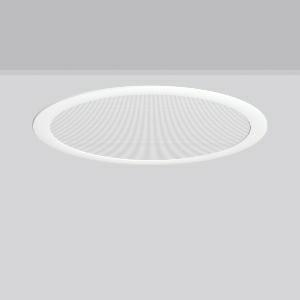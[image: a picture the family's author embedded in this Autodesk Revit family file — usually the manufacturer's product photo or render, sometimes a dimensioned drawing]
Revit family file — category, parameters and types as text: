
# Revit family: toledo_flat_round_e_901586_002_e46f
name_source: partatom
category: Lighting Fixtures
units: mm (PartAtom-declared; Revit-internal decimal feet)

## family parameters
Cut with Voids When Loaded = No
Host = Face
Light Source = No
Part Type = Normal
Room Calculation Point = No
Round Connector Dimension = Use Diameter
Shared = No

## types (1)
- TOLEDO FLAT round E (1 x LED Modul 830, 3450 lm, 3000)
    Apparent Load = 30 VA
    CIE Flux Codes = 62 86 96 100 100
    Color Rendering = 80
    Color Temperature = 3000
    Default Elevation = 1800 mm
    Description = Series: TOLEDO FLAT round
Ultra thin recessed downlight. Housing: die-cast aluminium. Lightguide and diffuser made of non-yellowing PMMA, prismatic. Ceiling installation with spring system. Mounting depth depends on ceiling strength. Including separate LED converter with connecting cable 250 mm. Suitable for through-wiring with separately available accessories. Surface mounted housing as accessory for all sizes. Retrofittable decorative cylinders made of chintz fabric as accessory, optional with satin finish plastic diffuser. Through-wiring box (5 pole) available as accessory. 
Colour: white
Diameter: 495 mm
Height: 6 mm
Cut-out diameter: 470 mm
Recess height: 40-59 mm
Luminaire: recess height: 31-51 mm
Lamp: LED
Socket: without socket
Colour temperature: 3000K
Colour rendering index (CRI): 80
System power: 30 W
Rated luminous flux: 3450 lm
Luminous efficiency: 115 lm/W
Control gear: Regulated power supply
Protection class: II
Type of protection: IP 54
    Height = 0 mm  [stored 0 ft]
    Lamp = 1 x LED Modul 830
    Lamp Light Flux = 3450 lm
    Lamp count = 1
    Length = 495 mm
    Lifetime = 50000 h
    Luminous efficacy = 115 lm/W
    Manufacturer = RZB
    ModVariant = No
    Model = 901586.002
    Mounting Place = Ceiling
    Mounting Type = Recessed
    Number of Poles = 1
    OnlyDefault = Yes
    Power Factor = 1
    Product Name = TOLEDO FLAT round E
    Product group = Recessed downlights
    ProductGroupID = 402
    Protection Class = Protection class II
    Protection Degree = IP 20
    RLX_Detail_Level = 1
    RLX_Emergency_Light_Flux = 0 lm
    RLX_Emergency_Type = 0
    RLX_Emergency_Type_DB = No
    RlxData = <blob elided: 38737 chars, md5=16fc7974>
    Socket = socket
    Standby Power = 0 W
    System Light Flux = 3450 lm
    System Power = 30 W
    Type Comments = Product without accessories
    Type Image = 901586.002.jpg
    URL = http://relux.com
    VarID = ---
    Voltage = 230 V
    Voltage Range = 220-240 V
    Weight = 0.00 kg
    Width = 0 mm  [stored 0 ft]

note: [stored X ft] marks values corroborated as IEEE doubles in the binary element streams (Revit-internal decimal feet)

## geometry (parser evidence)
native form markers: Blend x4, Sweep x9
no freeform markers — native parametric forms only
